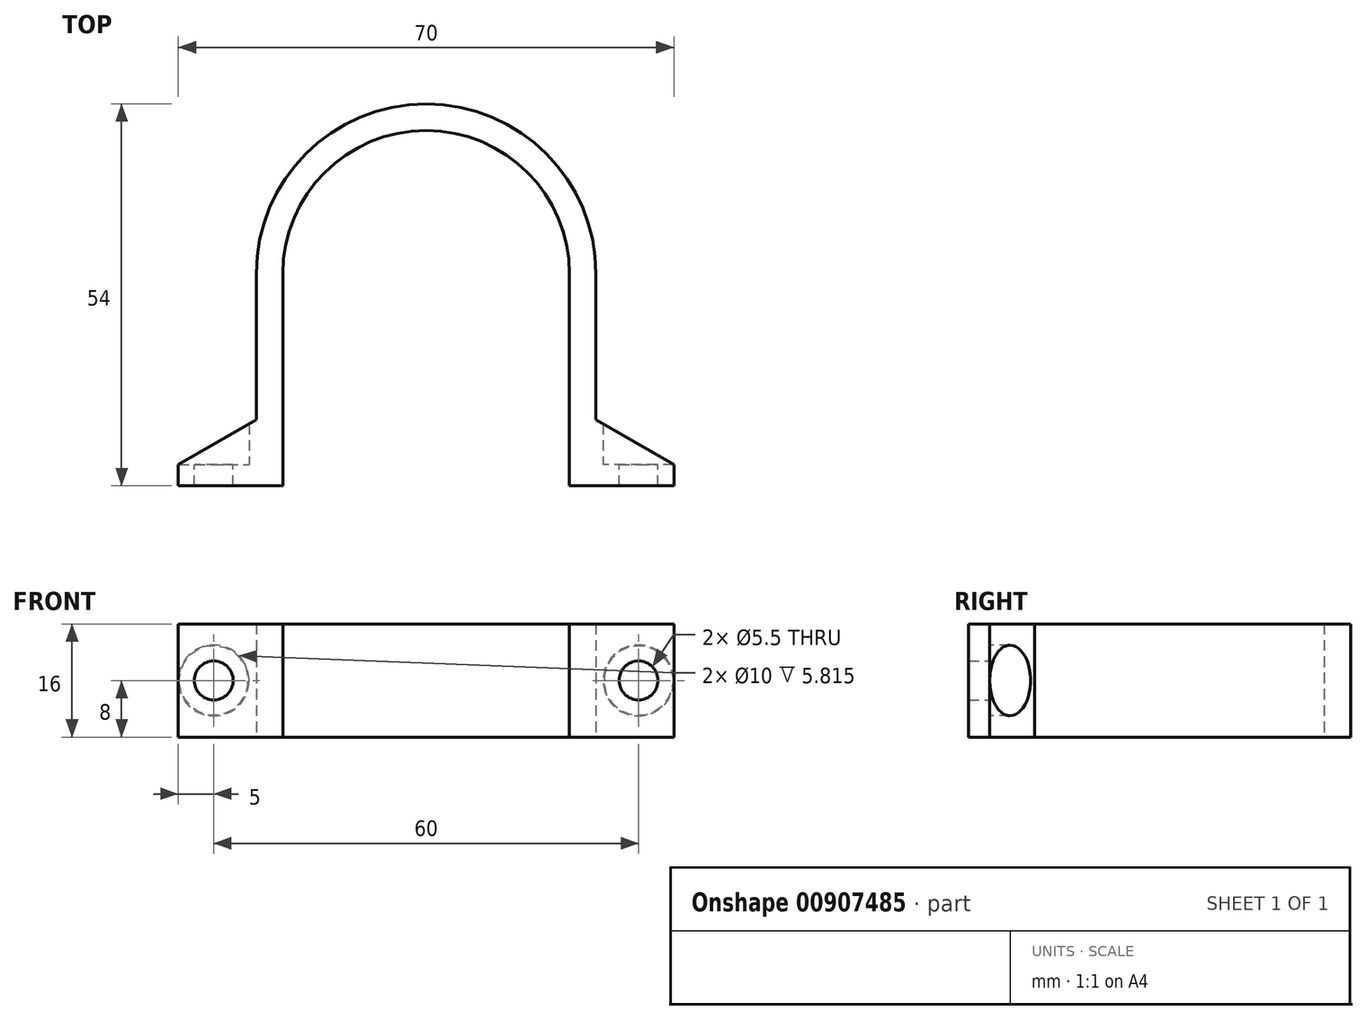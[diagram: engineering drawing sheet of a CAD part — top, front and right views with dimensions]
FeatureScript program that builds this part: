
annotation { "Feature Type Name" : "Feature", "Feature Type Description" : "" }
export const myFeature = defineFeature(function(context is Context, id is Id, definition is map)
    precondition{}
    {
        {
            var Q0;
            Q0=qCreatedBy(makeId("Top.planeOp"),FACE);
            var sketch = newSketch(context, id + "F0", { "sketchPlane" : qUnion([Q0])});
            skArc(sketch, "E0", {"start": v(20.25, 30) * mm, "mid": v(0, 50.25) * mm, "end": v(-20.25, 30) * mm});
            skArc(sketch, "E1", {"start": v(24, 30) * mm, "mid": v(0, 54) * mm, "end": v(-24, 30) * mm});
            skLineSegment(sketch, "E2", {"start": v(-24, 30) * mm, "end": v(-24, 9.35) * mm});
            skLineSegment(sketch, "E3", {"start": v(-24, 9.35) * mm, "end": v(-35, 3) * mm});
            skLineSegment(sketch, "E4", {"start": v(-35, 3) * mm, "end": v(-35, 0) * mm});
            skLineSegment(sketch, "E5", {"start": v(-35, 0) * mm, "end": v(-20.25, 0) * mm});
            skLineSegment(sketch, "E6", {"start": v(35, 0) * mm, "end": v(35, 3) * mm});
            skLineSegment(sketch, "E7", {"start": v(35, 3) * mm, "end": v(24, 9.35) * mm});
            skLineSegment(sketch, "E8", {"start": v(24, 9.35) * mm, "end": v(24, 30) * mm});
            skLineSegment(sketch, "E9", {"start": v(-20.25, 30) * mm, "end": v(-20.25, 0) * mm});
            skLineSegment(sketch, "E10", {"start": v(20.25, 30) * mm, "end": v(20.25, 0) * mm});
            skLineSegment(sketch, "E11.trimOffspring", {"start": v(20.25, 0) * mm, "end": v(35, 0) * mm});
            skSolve(sketch);
        }
        {
            var Q0;
            Q0=makeQuery(id+"F0.imprint","IMPRINT",FACE,{"disambiguationData":[TD([[makeQuery(id+"F0.imprint","IMPRINT",EDGE,{"derivedFrom":sQuery(id+"F0.wireOp",EDGE,"E0")}),-1.0]])]});
            extrude(context, id + "F1", {"entities" : qUnion([Q0]), "endBound" : BoundingType.SYMMETRIC, "depth" : 16 * mm, "offsetDistance" : 25 * mm});
        }
        {
            var Q0;
            Q0=makeQuery(id+"F1.opExtrude","CAP_VERTEX",VERTEX,{"disambiguationData":[OSD([sQuery(id+"F0.wireOp",EDGE,"E6"),sQuery(id+"F0.wireOp",EDGE,"E7")])],"isStart":false});
            var Q1;
            Q1=makeQuery(id+"F1.opExtrude","CAP_VERTEX",VERTEX,{"disambiguationData":[OSD([sQuery(id+"F0.wireOp",EDGE,"E3"),sQuery(id+"F0.wireOp",EDGE,"E4")])],"isStart":false});
            var Q2;
            Q2=makeQuery(id+"F1.opExtrude","CAP_VERTEX",VERTEX,{"disambiguationData":[OSD([sQuery(id+"F0.wireOp",EDGE,"E3"),sQuery(id+"F0.wireOp",EDGE,"E4")])],"isStart":true});
            cPlane(context, id + "F2", {"entities" : qUnion([Q0, Q1, Q2]), "cplaneType" : CPlaneType.THREE_POINT, "offset" : 25 * mm, "width" : 150 * mm, "height" : 150 * mm});
        }
        {
            var Q0;
            Q0=qCreatedBy(id+"F2.planeOp",FACE);
            var sketch = newSketch(context, id + "F3", { "sketchPlane" : qUnion([Q0])});
            skPoint(sketch, "E12", {"position": v(30, 0) * mm});
            skPoint(sketch, "E13", {"position": v(-30, 0) * mm});
            skSolve(sketch);
        }
        {
            var Q0;
            Q0=sQuery(id+"F3.wireOp",VERTEX,"E12");
            var Q1;
            Q1=sQuery(id+"F3.wireOp",VERTEX,"E13");
            var Q2;
            Q2=makeQuery(id+"F1.opExtrude","SWEPT_BODY",BODY,{"disambiguationData":[OSD([sQuery(id+"F0.wireOp",EDGE,"E0"),sQuery(id+"F0.wireOp",EDGE,"E1"),sQuery(id+"F0.wireOp",EDGE,"E2"),sQuery(id+"F0.wireOp",EDGE,"E3"),sQuery(id+"F0.wireOp",EDGE,"E4"),sQuery(id+"F0.wireOp",EDGE,"E5"),sQuery(id+"F0.wireOp",EDGE,"E6"),sQuery(id+"F0.wireOp",EDGE,"E7"),sQuery(id+"F0.wireOp",EDGE,"E8"),sQuery(id+"F0.wireOp",EDGE,"E9"),sQuery(id+"F0.wireOp",EDGE,"E10"),sQuery(id+"F0.wireOp",EDGE,"E11.trimOffspring")])]});
            hole(context, id + "F4", {"style" : HoleStyle.SIMPLE, "endStyle" : HoleEndStyle.THROUGH, "standardTappedOrClearance" : lookupTablePath({ "fit" : "Normal", "standard" : "ISO", "size" : "M5", "type" : "Clearance" }), "standardBlindInLast" : lookupTablePath({ "fit" : "Normal", "standard" : "ISO", "size" : "M5", "type" : "Clearance" }), "holeDiameter" : 5.5 * mm, "majorDiameter" : 8 * mm, "isTappedThrough" : true, "tappedDepth" : 16.25 * mm, "tapClearance" : 3, "startFromSketch" : true, "locations" : qUnion([Q0, Q1]), "scope" : qUnion([Q2])});
        }
        {
            var Q0;
            Q0=sQuery(id+"F3.wireOp",VERTEX,"E12");
            var Q1;
            Q1=sQuery(id+"F3.wireOp",VERTEX,"E13");
            var Q2;
            Q2=makeQuery(id+"F1.opExtrude","SWEPT_BODY",BODY,{"disambiguationData":[OSD([sQuery(id+"F0.wireOp",EDGE,"E0"),sQuery(id+"F0.wireOp",EDGE,"E1"),sQuery(id+"F0.wireOp",EDGE,"E2"),sQuery(id+"F0.wireOp",EDGE,"E3"),sQuery(id+"F0.wireOp",EDGE,"E4"),sQuery(id+"F0.wireOp",EDGE,"E5"),sQuery(id+"F0.wireOp",EDGE,"E6"),sQuery(id+"F0.wireOp",EDGE,"E7"),sQuery(id+"F0.wireOp",EDGE,"E8"),sQuery(id+"F0.wireOp",EDGE,"E9"),sQuery(id+"F0.wireOp",EDGE,"E10"),sQuery(id+"F0.wireOp",EDGE,"E11.trimOffspring")])]});
            hole(context, id + "F5", {"style" : HoleStyle.SIMPLE, "endStyle" : HoleEndStyle.THROUGH, "oppositeDirection" : true, "holeDiameter" : 10 * mm, "majorDiameter" : 5 * mm, "isTappedThrough" : true, "tappedDepth" : 16.25 * mm, "tapClearance" : 3, "startFromSketch" : true, "locations" : qUnion([Q0, Q1]), "scope" : qUnion([Q2])});
        }
    });
